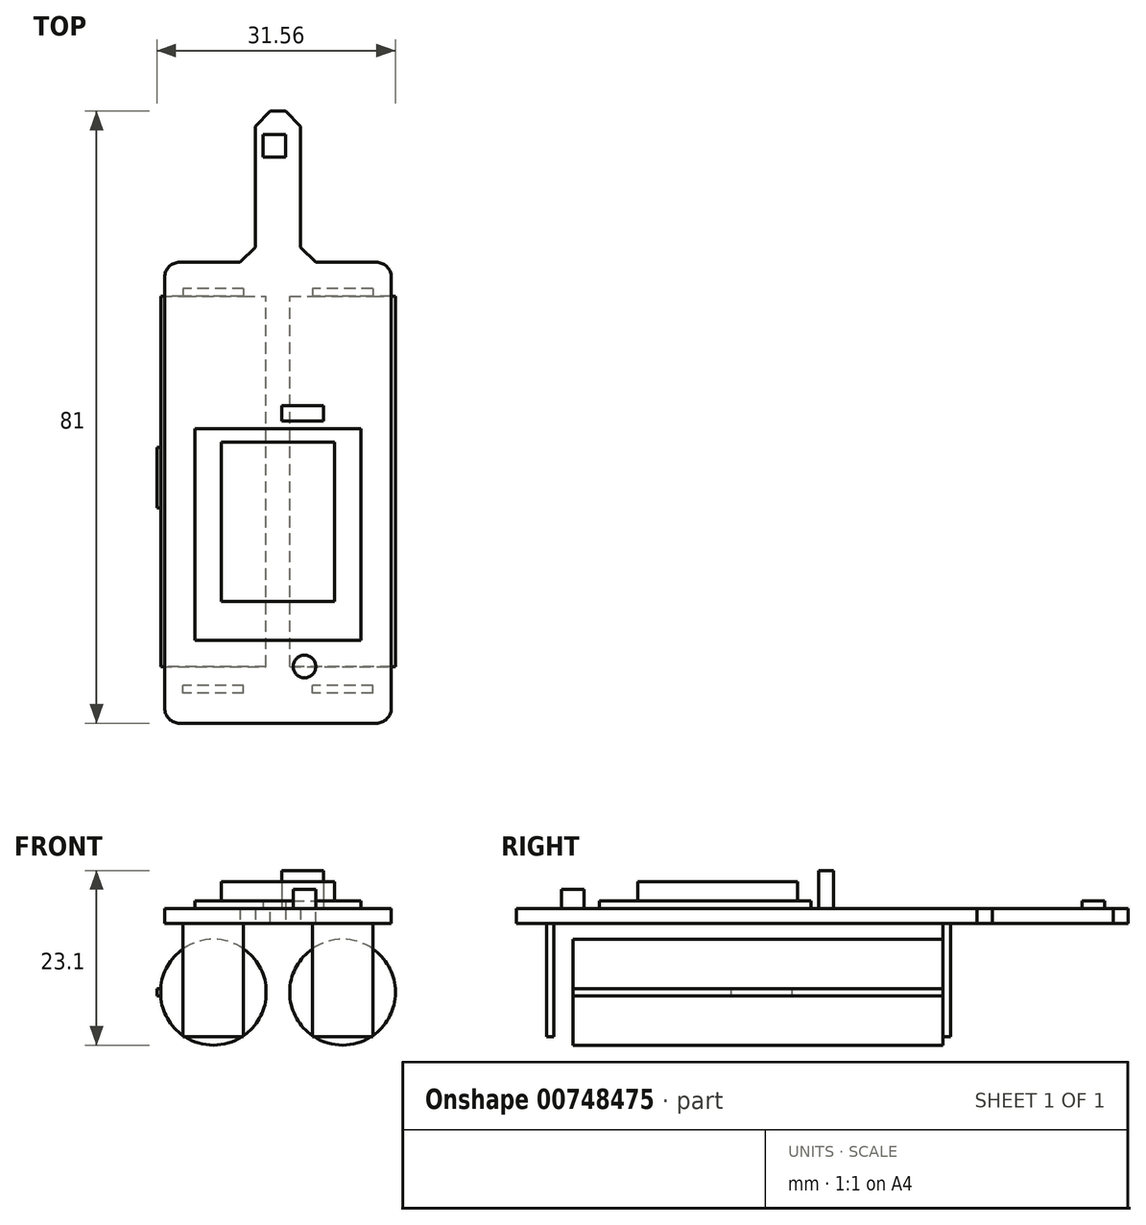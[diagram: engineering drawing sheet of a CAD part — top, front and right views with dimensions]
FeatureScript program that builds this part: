
annotation { "Feature Type Name" : "Feature", "Feature Type Description" : "" }
export const myFeature = defineFeature(function(context is Context, id is Id, definition is map)
    precondition{}
    {
        {
            var Q0;
            Q0=qCreatedBy(makeId("Top.planeOp"),FACE);
            var sketch = newSketch(context, id + "F0", { "sketchPlane" : qUnion([Q0])});
            skLineSegment(sketch, "E0", {"start": v(-15, 0) * mm, "end": v(15, 0) * mm});
            skLineSegment(sketch, "E1", {"start": v(15, 0) * mm, "end": v(15, 61) * mm});
            skLineSegment(sketch, "E2", {"start": v(15, 61) * mm, "end": v(3, 61) * mm});
            skLineSegment(sketch, "E3", {"start": v(3, 61) * mm, "end": v(3, 81) * mm});
            skLineSegment(sketch, "E4", {"start": v(3, 81) * mm, "end": v(-3, 81) * mm});
            skLineSegment(sketch, "E5", {"start": v(-3, 81) * mm, "end": v(-3, 61) * mm});
            skLineSegment(sketch, "E6", {"start": v(-3, 61) * mm, "end": v(-15, 61) * mm});
            skLineSegment(sketch, "E7", {"start": v(-15, 61) * mm, "end": v(-15, 0) * mm});
            skSolve(sketch);
        }
        {
            var Q0;
            Q0 = qSketchRegion(id + "F0", true);
            extrude(context, id + "F1", {"entities" : qUnion([Q0]), "depth" : 2 * mm, "offsetDistance" : 25 * mm});
        }
        {
            var Q0;
            Q0=makeQuery(id+"F1.opExtrude","CAP_FACE",FACE,{"disambiguationData":[OSD([sQuery(id+"F0.wireOp",EDGE,"E0"),sQuery(id+"F0.wireOp",EDGE,"E1"),sQuery(id+"F0.wireOp",EDGE,"E2"),sQuery(id+"F0.wireOp",EDGE,"E3"),sQuery(id+"F0.wireOp",EDGE,"E4"),sQuery(id+"F0.wireOp",EDGE,"E5"),sQuery(id+"F0.wireOp",EDGE,"E6"),sQuery(id+"F0.wireOp",EDGE,"E7")])],"isStart":false});
            var sketch = newSketch(context, id + "F2", { "sketchPlane" : qUnion([Q0])});
            skLineSegment(sketch, "E8", {"start": v(0, 0) * mm, "end": v(0, 11) * mm, "construction": true});
            skLineSegment(sketch, "E9.bottom", {"start": v(-11, 39) * mm, "end": v(11, 39) * mm});
            skLineSegment(sketch, "E9.top", {"start": v(-11, 11) * mm, "end": v(11, 11) * mm});
            skLineSegment(sketch, "E9.left", {"start": v(-11, 39) * mm, "end": v(-11, 11) * mm});
            skLineSegment(sketch, "E9.right", {"start": v(11, 39) * mm, "end": v(11, 11) * mm});
            skSolve(sketch);
        }
        {
            var Q0;
            Q0 = qSketchRegion(id + "F2", true);
            extrude(context, id + "F3", {"entities" : qUnion([Q0]), "operationType" : NewBodyOperationType.ADD, "depth" : 1 * mm, "offsetDistance" : 25 * mm});
        }
        {
            var Q0;
            Q0=makeQuery(id+"F3.opExtrude","CAP_FACE",FACE,{"disambiguationData":[OSD([sQuery(id+"F2.wireOp",EDGE,"E9.bottom"),sQuery(id+"F2.wireOp",EDGE,"E9.top"),sQuery(id+"F2.wireOp",EDGE,"E9.left"),sQuery(id+"F2.wireOp",EDGE,"E9.right")])],"isStart":false});
            var sketch = newSketch(context, id + "F4", { "sketchPlane" : qUnion([Q0])});
            skLineSegment(sketch, "E10", {"start": v(0, 11) * mm, "end": v(0, 16.1) * mm, "construction": true});
            skLineSegment(sketch, "E11.bottom", {"start": v(-7.5, 37.2) * mm, "end": v(7.5, 37.2) * mm});
            skLineSegment(sketch, "E11.top", {"start": v(-7.5, 16.1) * mm, "end": v(7.5, 16.1) * mm});
            skLineSegment(sketch, "E11.left", {"start": v(-7.5, 37.2) * mm, "end": v(-7.5, 16.1) * mm});
            skLineSegment(sketch, "E11.right", {"start": v(7.5, 37.2) * mm, "end": v(7.5, 16.1) * mm});
            skSolve(sketch);
        }
        {
            var Q0;
            Q0 = qSketchRegion(id + "F4", true);
            extrude(context, id + "F5", {"entities" : qUnion([Q0]), "operationType" : NewBodyOperationType.ADD, "depth" : 2.5 * mm, "offsetDistance" : 25 * mm});
        }
        {
            var Q0;
            Q0=makeQuery(id+"F1.opExtrude","CAP_FACE",FACE,{"disambiguationData":[OSD([sQuery(id+"F0.wireOp",EDGE,"E0"),sQuery(id+"F0.wireOp",EDGE,"E1"),sQuery(id+"F0.wireOp",EDGE,"E2"),sQuery(id+"F0.wireOp",EDGE,"E3"),sQuery(id+"F0.wireOp",EDGE,"E4"),sQuery(id+"F0.wireOp",EDGE,"E5"),sQuery(id+"F0.wireOp",EDGE,"E6"),sQuery(id+"F0.wireOp",EDGE,"E7")])],"isStart":false});
            var sketch = newSketch(context, id + "F6", { "sketchPlane" : qUnion([Q0])});
            skLineSegment(sketch, "E12.bottom", {"start": v(0.5, 42) * mm, "end": v(6, 42) * mm});
            skLineSegment(sketch, "E12.top", {"start": v(0.5, 40) * mm, "end": v(6, 40) * mm});
            skLineSegment(sketch, "E12.left", {"start": v(0.5, 42) * mm, "end": v(0.5, 40) * mm});
            skLineSegment(sketch, "E12.right", {"start": v(6, 42) * mm, "end": v(6, 40) * mm});
            skSolve(sketch);
        }
        {
            var Q0;
            Q0 = qSketchRegion(id + "F6", true);
            extrude(context, id + "F7", {"entities" : qUnion([Q0]), "operationType" : NewBodyOperationType.ADD, "depth" : 5 * mm, "offsetDistance" : 25 * mm});
        }
        {
            var Q0;
            Q0=makeQuery(id+"F1.opExtrude","CAP_FACE",FACE,{"disambiguationData":[OSD([sQuery(id+"F0.wireOp",EDGE,"E0"),sQuery(id+"F0.wireOp",EDGE,"E1"),sQuery(id+"F0.wireOp",EDGE,"E2"),sQuery(id+"F0.wireOp",EDGE,"E3"),sQuery(id+"F0.wireOp",EDGE,"E4"),sQuery(id+"F0.wireOp",EDGE,"E5"),sQuery(id+"F0.wireOp",EDGE,"E6"),sQuery(id+"F0.wireOp",EDGE,"E7")])],"isStart":false});
            var sketch = newSketch(context, id + "F8", { "sketchPlane" : qUnion([Q0])});
            skLineSegment(sketch, "E13.bottom", {"start": v(-2, 77.9) * mm, "end": v(1, 77.9) * mm});
            skLineSegment(sketch, "E13.top", {"start": v(-2, 74.9) * mm, "end": v(1, 74.9) * mm});
            skLineSegment(sketch, "E13.left", {"start": v(-2, 77.9) * mm, "end": v(-2, 74.9) * mm});
            skLineSegment(sketch, "E13.right", {"start": v(1, 77.9) * mm, "end": v(1, 74.9) * mm});
            skSolve(sketch);
        }
        {
            var Q0;
            Q0 = qSketchRegion(id + "F8", true);
            extrude(context, id + "F9", {"entities" : qUnion([Q0]), "operationType" : NewBodyOperationType.ADD, "depth" : 1 * mm, "offsetDistance" : 25 * mm});
        }
        {
            var Q0;
            Q0=makeQuery(id+"F1.opExtrude","CAP_FACE",FACE,{"disambiguationData":[OSD([sQuery(id+"F0.wireOp",EDGE,"E0"),sQuery(id+"F0.wireOp",EDGE,"E1"),sQuery(id+"F0.wireOp",EDGE,"E2"),sQuery(id+"F0.wireOp",EDGE,"E3"),sQuery(id+"F0.wireOp",EDGE,"E4"),sQuery(id+"F0.wireOp",EDGE,"E5"),sQuery(id+"F0.wireOp",EDGE,"E6"),sQuery(id+"F0.wireOp",EDGE,"E7")])],"isStart":false});
            var sketch = newSketch(context, id + "F10", { "sketchPlane" : qUnion([Q0])});
            skCircle(sketch, "E14", {"center": v(3.5, 7.5) * mm, "radius": 1.5 * mm});
            skSolve(sketch);
        }
        {
            var Q0;
            Q0 = qSketchRegion(id + "F10", true);
            extrude(context, id + "F11", {"entities" : qUnion([Q0]), "operationType" : NewBodyOperationType.ADD, "depth" : 2.5 * mm, "offsetDistance" : 25 * mm});
        }
        {
            var Q0;
            Q0=makeQuery(id+"F1.opExtrude","CAP_FACE",FACE,{"disambiguationData":[OSD([sQuery(id+"F0.wireOp",EDGE,"E0"),sQuery(id+"F0.wireOp",EDGE,"E1"),sQuery(id+"F0.wireOp",EDGE,"E2"),sQuery(id+"F0.wireOp",EDGE,"E3"),sQuery(id+"F0.wireOp",EDGE,"E4"),sQuery(id+"F0.wireOp",EDGE,"E5"),sQuery(id+"F0.wireOp",EDGE,"E6"),sQuery(id+"F0.wireOp",EDGE,"E7")])],"isStart":true});
            var sketch = newSketch(context, id + "F12", { "sketchPlane" : qUnion([Q0])});
            skLineSegment(sketch, "E15.bottom", {"start": v(15, 0) * mm, "end": v(-15, 0) * mm, "construction": true});
            skLineSegment(sketch, "E15.top", {"start": v(15, -4) * mm, "end": v(-15, -4) * mm, "construction": true});
            skLineSegment(sketch, "E15.left", {"start": v(15, 0) * mm, "end": v(15, -4) * mm, "construction": true});
            skLineSegment(sketch, "E15.right", {"start": v(-15, 0) * mm, "end": v(-15, -4) * mm, "construction": true});
            skLineSegment(sketch, "E16.bottom", {"start": v(12.55, -4) * mm, "end": v(4.55, -4) * mm});
            skLineSegment(sketch, "E16.top", {"start": v(12.55, -5) * mm, "end": v(4.55, -5) * mm});
            skLineSegment(sketch, "E16.left", {"start": v(12.55, -4) * mm, "end": v(12.55, -5) * mm});
            skLineSegment(sketch, "E16.right", {"start": v(4.55, -4) * mm, "end": v(4.55, -5) * mm});
            skLineSegment(sketch, "E17.bottom", {"start": v(-4.55, -4) * mm, "end": v(-12.55, -4) * mm});
            skLineSegment(sketch, "E17.top", {"start": v(-4.55, -5) * mm, "end": v(-12.55, -5) * mm});
            skLineSegment(sketch, "E17.left", {"start": v(-4.55, -4) * mm, "end": v(-4.55, -5) * mm});
            skLineSegment(sketch, "E17.right", {"start": v(-12.55, -4) * mm, "end": v(-12.55, -5) * mm});
            skLineSegment(sketch, "E18", {"start": v(4.55, -5) * mm, "end": v(-4.55, -5) * mm, "construction": true});
            skLineSegment(sketch, "E19", {"start": v(0, 0) * mm, "end": v(0, -5) * mm, "construction": true});
            skPoint(sketch, "E19.endSnap0", {"position": v(0, -4) * mm});
            skLineSegment(sketch, "E20.bottom", {"start": v(15, -61) * mm, "end": v(-15, -61) * mm, "construction": true});
            skLineSegment(sketch, "E20.top", {"start": v(15, -57.5) * mm, "end": v(-15, -57.5) * mm, "construction": true});
            skLineSegment(sketch, "E20.left", {"start": v(15, -61) * mm, "end": v(15, -57.5) * mm, "construction": true});
            skLineSegment(sketch, "E20.right", {"start": v(-15, -61) * mm, "end": v(-15, -57.5) * mm, "construction": true});
            skLineSegment(sketch, "E21", {"start": v(0, -61) * mm, "end": v(0, -56.5) * mm, "construction": true});
            skLineSegment(sketch, "E22.bottom", {"start": v(12.55, -57.5) * mm, "end": v(4.55, -57.5) * mm});
            skLineSegment(sketch, "E22.top", {"start": v(12.55, -56.5) * mm, "end": v(4.55, -56.5) * mm});
            skLineSegment(sketch, "E22.left", {"start": v(12.55, -57.5) * mm, "end": v(12.55, -56.5) * mm});
            skLineSegment(sketch, "E22.right", {"start": v(4.55, -57.5) * mm, "end": v(4.55, -56.5) * mm});
            skLineSegment(sketch, "E23.bottom", {"start": v(-4.55, -57.5) * mm, "end": v(-12.55, -57.5) * mm});
            skLineSegment(sketch, "E23.top", {"start": v(-4.55, -56.5) * mm, "end": v(-12.55, -56.5) * mm});
            skLineSegment(sketch, "E23.left", {"start": v(-4.55, -57.5) * mm, "end": v(-4.55, -56.5) * mm});
            skLineSegment(sketch, "E23.right", {"start": v(-12.55, -57.5) * mm, "end": v(-12.55, -56.5) * mm});
            skLineSegment(sketch, "E24", {"start": v(4.55, -56.5) * mm, "end": v(-4.55, -56.5) * mm, "construction": true});
            skSolve(sketch);
        }
        {
            var Q0;
            Q0 = qSketchRegion(id + "F12", true);
            extrude(context, id + "F13", {"entities" : qUnion([Q0]), "operationType" : NewBodyOperationType.ADD, "depth" : 15 * mm, "offsetDistance" : 25 * mm});
        }
        {
            var Q0;
            Q0=makeQuery(id+"F13.opExtrude","SWEPT_FACE",FACE,{"disambiguationData":[OSD([sQuery(id+"F12.wireOp",EDGE,"E22.top")])]});
            var sketch = newSketch(context, id + "F14", { "sketchPlane" : qUnion([Q0])});
            skLineSegment(sketch, "E25", {"start": v(8.55, -15) * mm, "end": v(8.55, 0) * mm, "construction": true});
            skArc(sketch, "E26", {"start": v(15.53, -8.6) * mm, "mid": v(8.55, -2.1) * mm, "end": v(1.57, -8.6) * mm});
            skLineSegment(sketch, "E27", {"start": v(1.57, -9.6) * mm, "end": v(1.57, -8.6) * mm});
            skLineSegment(sketch, "E28", {"start": v(15.53, -9.6) * mm, "end": v(15.53, -8.6) * mm});
            skArc(sketch, "E29.trimOffspring", {"start": v(1.57, -9.6) * mm, "mid": v(8.55, -16.1) * mm, "end": v(15.53, -9.6) * mm});
            skLineSegment(sketch, "E30.MirrorCS", {"start": v(29.5, -9.6) * mm, "end": v(29.5, -8.6) * mm});
            skArc(sketch, "E31.MirrorCS", {"start": v(-1.57, -9.6) * mm, "mid": v(-8.55, -16.1) * mm, "end": v(-15.53, -9.6) * mm});
            skLineSegment(sketch, "E32.MirrorCS", {"start": v(-15.53, -9.6) * mm, "end": v(-15.53, -8.6) * mm});
            skLineSegment(sketch, "E33.MirrorCS", {"start": v(-1.57, -9.6) * mm, "end": v(-1.57, -8.6) * mm});
            skArc(sketch, "E34.MirrorCS", {"start": v(-15.53, -8.6) * mm, "mid": v(-8.55, -2.1) * mm, "end": v(-1.57, -8.6) * mm});
            skSolve(sketch);
        }
        {
            var Q0;
            Q0 = qSketchRegion(id + "F14", true);
            extrude(context, id + "F15", {"entities" : qUnion([Q0]), "operationType" : NewBodyOperationType.ADD, "depth" : 49 * mm, "offsetDistance" : 25 * mm});
        }
        {
            var Q0;
            Q0=makeQuery(id+"F1.opExtrude","SWEPT_EDGE",EDGE,{"disambiguationData":[OSD([sQuery(id+"F0.wireOp",EDGE,"E5"),sQuery(id+"F0.wireOp",EDGE,"E6")])]});
            var Q1;
            Q1=makeQuery(id+"F1.opExtrude","SWEPT_EDGE",EDGE,{"disambiguationData":[OSD([sQuery(id+"F0.wireOp",EDGE,"E2"),sQuery(id+"F0.wireOp",EDGE,"E3")])]});
            var Q2;
            Q2=makeQuery(id+"F1.opExtrude","SWEPT_EDGE",EDGE,{"disambiguationData":[OSD([sQuery(id+"F0.wireOp",EDGE,"E3"),sQuery(id+"F0.wireOp",EDGE,"E4")])]});
            var Q3;
            Q3=makeQuery(id+"F1.opExtrude","SWEPT_EDGE",EDGE,{"disambiguationData":[OSD([sQuery(id+"F0.wireOp",EDGE,"E4"),sQuery(id+"F0.wireOp",EDGE,"E5")])]});
            chamfer(context, id + "F16", {"entities" : qUnion([Q0, Q1, Q2, Q3]), "width" : 2 * mm, "tangentPropagation" : true});
        }
        {
            var Q0;
            Q0=makeQuery(id+"F1.opExtrude","SWEPT_EDGE",EDGE,{"disambiguationData":[OSD([sQuery(id+"F0.wireOp",EDGE,"E1"),sQuery(id+"F0.wireOp",EDGE,"E2")])]});
            var Q1;
            Q1=makeQuery(id+"F1.opExtrude","SWEPT_EDGE",EDGE,{"disambiguationData":[OSD([sQuery(id+"F0.wireOp",EDGE,"E6"),sQuery(id+"F0.wireOp",EDGE,"E7")])]});
            var Q2;
            Q2=makeQuery(id+"F1.opExtrude","SWEPT_EDGE",EDGE,{"disambiguationData":[OSD([sQuery(id+"F0.wireOp",EDGE,"E0"),sQuery(id+"F0.wireOp",EDGE,"E1")])]});
            var Q3;
            Q3=makeQuery(id+"F1.opExtrude","SWEPT_EDGE",EDGE,{"disambiguationData":[OSD([sQuery(id+"F0.wireOp",EDGE,"E0"),sQuery(id+"F0.wireOp",EDGE,"E7")])]});
            fillet(context, id + "F17", {"entities" : qUnion([Q0, Q1, Q2, Q3]), "radius" : 2 * mm, "tangentPropagation" : true, "allowEdgeOverflow" : false});
        }
        {
            var Q0;
            Q0=makeQuery(id+"F15.opExtrude","SWEPT_FACE",FACE,{"disambiguationData":[OSD([sQuery(id+"F14.wireOp",EDGE,"E32.MirrorCS")])]});
            var sketch = newSketch(context, id + "F18", { "sketchPlane" : qUnion([Q0])});
            skLineSegment(sketch, "E35.bottom", {"start": v(-36.52, -9.6) * mm, "end": v(-28.48, -9.6) * mm});
            skLineSegment(sketch, "E35.top", {"start": v(-36.52, -8.6) * mm, "end": v(-28.48, -8.6) * mm});
            skLineSegment(sketch, "E35.left", {"start": v(-36.52, -9.6) * mm, "end": v(-36.52, -8.6) * mm});
            skLineSegment(sketch, "E35.right", {"start": v(-28.48, -9.6) * mm, "end": v(-28.48, -8.6) * mm});
            skSolve(sketch);
        }
        {
            var Q0;
            Q0=makeQuery(id+"F18.imprint","IMPRINT",FACE,{"disambiguationData":[TD([[makeQuery(id+"F18.imprint","IMPRINT",EDGE,{"derivedFrom":sQuery(id+"F18.wireOp",EDGE,"E35.bottom")}),-1.0]])]});
            extrude(context, id + "F19", {"entities" : qUnion([Q0]), "operationType" : NewBodyOperationType.ADD, "depth" : .5 * mm, "offsetDistance" : 25 * mm});
        }
    });
